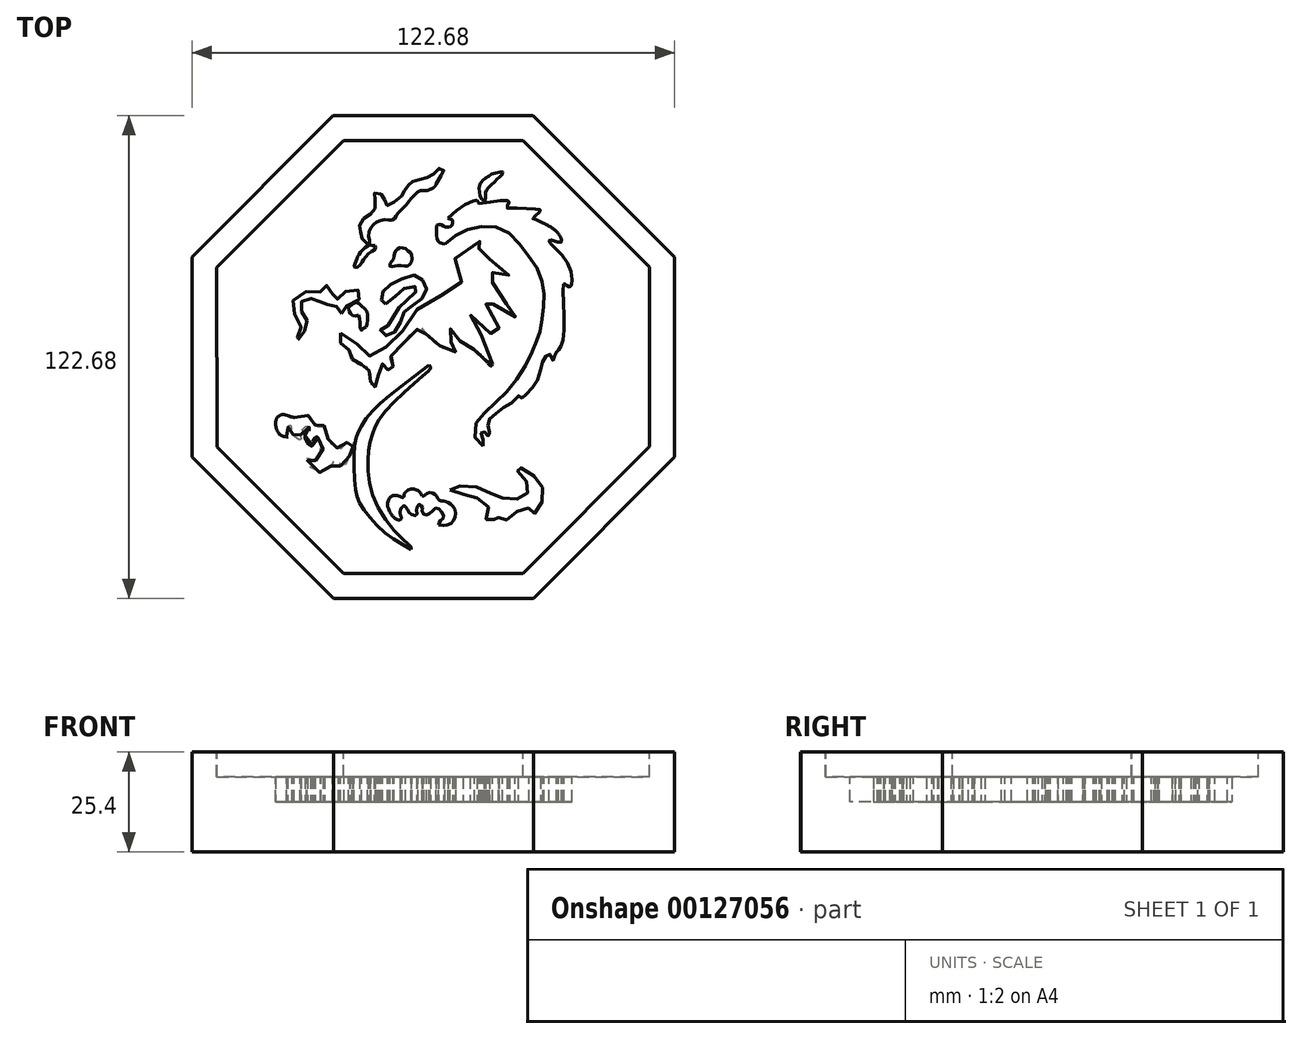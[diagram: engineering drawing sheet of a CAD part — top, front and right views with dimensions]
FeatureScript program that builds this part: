
annotation { "Feature Type Name" : "Feature", "Feature Type Description" : "" }
export const myFeature = defineFeature(function(context is Context, id is Id, definition is map)
    precondition{}
    {
        {
            var Q0;
            Q0=qCreatedBy(makeId("Top.planeOp"),FACE);
            var sketch = newSketch(context, id + "F0", { "sketchPlane" : qUnion([Q0])});
            skCircle(sketch, "E0.cCircle", {"center": v(0, 0) * mm, "radius": 61.32 * mm, "construction": true});
            skLineSegment(sketch, "E0.0", {"start": v(-61.3, -25.44) * mm, "end": v(-61.34, 25.36) * mm});
            skLineSegment(sketch, "E0.1", {"start": v(-61.34, 25.36) * mm, "end": v(-25.44, 61.3) * mm});
            skLineSegment(sketch, "E0.2", {"start": v(-25.44, 61.3) * mm, "end": v(25.36, 61.34) * mm});
            skLineSegment(sketch, "E0.3", {"start": v(25.36, 61.34) * mm, "end": v(61.3, 25.44) * mm});
            skLineSegment(sketch, "E0.4", {"start": v(61.3, 25.44) * mm, "end": v(61.34, -25.36) * mm});
            skLineSegment(sketch, "E0.5", {"start": v(61.34, -25.36) * mm, "end": v(25.44, -61.3) * mm});
            skLineSegment(sketch, "E0.6", {"start": v(25.44, -61.3) * mm, "end": v(-25.36, -61.34) * mm});
            skLineSegment(sketch, "E0.7", {"start": v(-25.36, -61.34) * mm, "end": v(-61.3, -25.44) * mm});
            skPoint(sketch, "E0.0.midPoint", {"position": v(-61.32, -0.04) * mm});
            skSolve(sketch);
        }
        {
            var Q0;
            Q0=qSketchRegion(id+"F0",true);
            extrude(context, id + "F1", {"entities" : qUnion([Q0]), "depth" : 25.4 * mm});
        }
        {
            var Q0;
            Q0=makeQuery(id+"F1.opExtrude","CAP_FACE",FACE,{"disambiguationData":[OSD([sQuery(id+"F0.wireOp",EDGE,"E0.0"),sQuery(id+"F0.wireOp",EDGE,"E0.1"),sQuery(id+"F0.wireOp",EDGE,"E0.2"),sQuery(id+"F0.wireOp",EDGE,"E0.3"),sQuery(id+"F0.wireOp",EDGE,"E0.4"),sQuery(id+"F0.wireOp",EDGE,"E0.5"),sQuery(id+"F0.wireOp",EDGE,"E0.6"),sQuery(id+"F0.wireOp",EDGE,"E0.7")])],"isStart":false});
            var sketch = newSketch(context, id + "F2", { "sketchPlane" : qUnion([Q0])});
            skLineSegment(sketch, "E1.0", {"start": v(-54.96, -22.8) * mm, "end": v(-54.99, 22.73) * mm});
            skLineSegment(sketch, "E1.1", {"start": v(-22.73, -54.99) * mm, "end": v(-54.96, -22.8) * mm});
            skLineSegment(sketch, "E1.2", {"start": v(-54.99, 22.73) * mm, "end": v(-22.8, 54.96) * mm});
            skLineSegment(sketch, "E1.3", {"start": v(22.8, -54.96) * mm, "end": v(-22.73, -54.99) * mm});
            skLineSegment(sketch, "E1.4", {"start": v(-22.8, 54.96) * mm, "end": v(22.73, 54.99) * mm});
            skLineSegment(sketch, "E1.5", {"start": v(22.73, 54.99) * mm, "end": v(54.96, 22.8) * mm});
            skLineSegment(sketch, "E1.6", {"start": v(54.96, 22.8) * mm, "end": v(54.99, -22.73) * mm});
            skLineSegment(sketch, "E1.7", {"start": v(54.99, -22.73) * mm, "end": v(22.8, -54.96) * mm});
            skSolve(sketch);
        }
        {
            var Q0;
            Q0=qSketchRegion(id+"F2",true);
            extrude(context, id + "F3", {"entities" : qUnion([Q0]), "operationType" : NewBodyOperationType.REMOVE, "oppositeDirection" : true, "depth" : 6.35 * mm});
        }
        {
            var Q0;
            Q0=makeQuery(id+"F3.boolean.opBoolean","COPY",FACE,{"derivedFrom":makeQuery(id+"F3.opExtrude","CAP_FACE",FACE,{"disambiguationData":[OSD([sQuery(id+"F2.wireOp",EDGE,"E1.0"),sQuery(id+"F2.wireOp",EDGE,"E1.1"),sQuery(id+"F2.wireOp",EDGE,"E1.2"),sQuery(id+"F2.wireOp",EDGE,"E1.3"),sQuery(id+"F2.wireOp",EDGE,"E1.4"),sQuery(id+"F2.wireOp",EDGE,"E1.5"),sQuery(id+"F2.wireOp",EDGE,"E1.6"),sQuery(id+"F2.wireOp",EDGE,"E1.7")])],"isStart":false})});
            var sketch = newSketch(context, id + "F4", { "sketchPlane" : qUnion([Q0])});
            skFitSpline(sketch, "E2", {"points": [v(-1.1, -2.1) * mm, v(-15.28, -13.56) * mm, v(-18.94, -18.81) * mm, v(-20.03, -22.74) * mm, v(-19.8, -33.28) * mm, v(-18.48, -37.41) * mm, v(-13.16, -43.92) * mm, v(-5.64, -48.87) * mm], "startDerivative": vector(-92.7, -70.76) * mm, "endDerivative": vector(49.7, -26.65) * mm});
            skFitSpline(sketch, "E3", {"points": [v(-1.1, -2.1) * mm, v(-0.63, -2.66) * mm, v(-2.57, -4.73) * mm, v(-12.47, -14.06) * mm, v(-15.53, -19.76) * mm, v(-16.6, -26.27) * mm, v(-13.9, -38.48) * mm, v(-6.27, -47.68) * mm, v(-5.64, -48.3) * mm, v(-5.64, -48.87) * mm], "startDerivative": vector(15.8, -12.08) * mm, "endDerivative": vector(-1.9, -16.76) * mm});
            skFitSpline(sketch, "E4", {"points": [v(-23.56, 6.14) * mm, v(-22.79, 5.01) * mm, v(-21, 4.18) * mm, v(-19.5, 3.43) * mm, v(-18.43, 1.99) * mm, v(-17.94, 0.65) * mm, v(-17.3, 0) * mm, v(-14.98, 0.65) * mm, v(-14.07, 0.65) * mm, v(-12.95, 1.64) * mm, v(-11.75, 2.76) * mm, v(-10.14, 4.24) * mm, v(-9.01, 5.22) * mm, v(-7.25, 7.4) * mm, v(-5.78, 10.07) * mm, v(-4.65, 11.62) * mm, v(-2.2, 13.44) * mm, v(0, 14.85) * mm, v(3.36, 15.97) * mm, v(4.98, 16.19) * mm, v(7.08, 18.79) * mm, v(7.36, 22.72) * mm, v(6.33, 24.4) * mm, v(5.33, 25.33) * mm, v(9.1, 28.92) * mm, v(12.6, 29.34) * mm, v(14.27, 29.34) * mm, v(12.35, 28.27) * mm, v(11.37, 27.15) * mm, v(11.16, 25.95) * mm, v(12.64, 25.18) * mm, v(14.32, 24.83) * mm, v(17.2, 23.5) * mm, v(18.54, 21.95) * mm, v(19.31, 20.26) * mm, v(18.6, 20.4) * mm, v(17, 20.96) * mm, v(14.81, 21.46) * mm, v(13.48, 20.75) * mm, v(13.34, 20.05) * mm, v(13.69, 19.63) * mm, v(15.66, 18.5) * mm, v(17.27, 16.4) * mm, v(18.33, 14) * mm, v(20.09, 12.04) * mm, v(21.5, 10.84) * mm, v(21.5, 10.28) * mm, v(20.37, 10.28) * mm, v(18.05, 11.05) * mm, v(15.52, 13.1) * mm, v(14.46, 14.36) * mm, v(13.48, 15.06) * mm, v(12.99, 14.92) * mm, v(13.34, 13.51) * mm, v(14.6, 11.2) * mm, v(16.43, 9.02) * mm, v(16.64, 4.59) * mm, v(16.71, 3.96) * mm, v(15.52, 5.01) * mm, v(12.28, 8.17) * mm, v(10.25, 10.42) * mm, v(9.47, 10.63) * mm, v(9.61, 9.23) * mm, v(10.74, 7.61) * mm, v(12.28, 5.43) * mm, v(13.55, 3.75) * mm, v(15.1, -1.8) * mm], "startDerivative": vector(44.12, -97.76) * mm, "endDerivative": vector(53.66, -252.27) * mm});
            skFitSpline(sketch, "E5", {"points": [v(-23.56, 6.14) * mm, v(-23.97, 5.3) * mm, v(-24, 4.48) * mm, v(-23.56, 3.64) * mm, v(-22.79, 2.98) * mm, v(-22.5, 2.67) * mm, v(-21.65, 1.95) * mm, v(-20.68, 1.41) * mm, v(-20.65, 0.63) * mm, v(-20.62, -0.28) * mm, v(-20.21, -1.4) * mm, v(-19, -1.8) * mm, v(-18.27, -1.84) * mm, v(-17.37, -2.22) * mm, v(-16.77, -2.6) * mm, v(-16.43, -3.22) * mm, v(-16.18, -3.78) * mm, v(-15.86, -4.75) * mm, v(-15.99, -6.04) * mm, v(-15.83, -7.38) * mm, v(-15.83, -7.7) * mm, v(-15.42, -7.73) * mm, v(-14.64, -7.44) * mm, v(-14.08, -5.91) * mm, v(-14.08, -4.9) * mm, v(-13.55, -3.69) * mm, v(-13.67, -2.56) * mm, v(-12.95, -1.78) * mm, v(-12.51, -1.75) * mm, v(-12.14, -2.25) * mm, v(-11.82, -2.62) * mm, v(-11.42, -3.4) * mm, v(-11.23, -3.72) * mm, v(-10.32, -3.4) * mm, v(-10.2, -2.72) * mm, v(-10.45, -1.68) * mm, v(-10.98, -0.59) * mm, v(-10.89, 0) * mm, v(-10.42, 0.76) * mm, v(-8.32, 2.6) * mm, v(-6.16, 5.36) * mm, v(-4.15, 7.02) * mm, v(-3.3, 7.55) * mm, v(-2.18, 6.58) * mm, v(-1.3, 5.01) * mm, v(0.82, 3.58) * mm, v(3.2, 1.92) * mm, v(5.49, 1.32) * mm, v(5.74, 1.38) * mm, v(5.43, 1.92) * mm, v(4.92, 2.92) * mm, v(4.33, 4.36) * mm, v(4.14, 6.42) * mm, v(4.33, 7.14) * mm, v(4.58, 6.92) * mm, v(5.7, 5.45) * mm, v(7.59, 3.42) * mm, v(9.5, 2.57) * mm, v(10.68, 1.6) * mm, v(12.22, 0.26) * mm, v(13.66, -1.28) * mm, v(14.28, -2.03) * mm, v(14.66, -2.31) * mm, v(15.1, -1.8) * mm], "startDerivative": vector(-33.8, -56.96) * mm, "endDerivative": vector(35.19, 59.41) * mm});
            skFitSpline(sketch, "E6", {"points": [v(3.02, 28.65) * mm, v(5.32, 30.69) * mm, v(7.88, 32.02) * mm, v(10.9, 32.95) * mm, v(14.44, 33.25) * mm, v(17.73, 32.4) * mm, v(20.66, 30.25) * mm, v(22.82, 27.45) * mm, v(25.17, 24.43) * mm, v(26.96, 21.56) * mm, v(27.82, 18.27) * mm, v(28.13, 15.75) * mm, v(27.98, 13.3) * mm, v(27.83, 10.88) * mm, v(27.4, 8.1) * mm, v(26.94, 5.85) * mm, v(26.35, 4.26) * mm, v(25.69, 2.62) * mm, v(24.16, -0.73) * mm, v(22.41, -3.85) * mm, v(19.64, -7.82) * mm, v(17.33, -10.23) * mm, v(14.4, -12.82) * mm, v(11.7, -15.6) * mm, v(10.6, -17.65) * mm, v(10.86, -21.09) * mm, v(12.7, -22.63) * mm], "startDerivative": vector(58.67, 60.1) * mm, "endDerivative": vector(54.1, -50.25) * mm});
            skFitSpline(sketch, "E7", {"points": [v(3.02, 28.65) * mm, v(1.21, 29.42) * mm, v(0.86, 31.3) * mm, v(0.86, 33.34) * mm, v(1.65, 33.7) * mm, v(3.02, 33.08) * mm, v(3.77, 33.02) * mm, v(4.67, 33.34) * mm, v(4.84, 34.4) * mm, v(4.58, 35.03) * mm, v(3.77, 35.11) * mm, v(3.77, 35.26) * mm], "startDerivative": vector(-14.7, 5.6) * mm, "endDerivative": vector(3.92, 12.76) * mm});
            skFitSpline(sketch, "E8", {"points": [v(12.7, -22.63) * mm, v(12.7, -21.63) * mm, v(12.7, -20.6) * mm, v(12.09, -19.6) * mm, v(12.7, -18.76) * mm, v(12.88, -18.81) * mm, v(13.13, -19.2) * mm, v(13.64, -19.76) * mm, v(13.97, -20.1) * mm, v(14.17, -20.15) * mm, v(14.33, -19.37) * mm, v(14.1, -18.73) * mm, v(13.89, -17.28) * mm, v(14.14, -16.25) * mm, v(14.44, -15.44) * mm, v(16.26, -14.21) * mm, v(17.7, -12.93) * mm, v(19.46, -11.92) * mm, v(21.25, -10.53) * mm, v(21.97, -9.47) * mm, v(22.48, -10.33) * mm, v(22.92, -10.22) * mm, v(23.45, -9.6) * mm, v(24.71, -8.3) * mm, v(26.14, -6.56) * mm, v(26.77, -5.21) * mm, v(27.5, -2.3) * mm, v(27.8, -1.3) * mm, v(28.3, -0.29) * mm, v(28.95, 0.66) * mm, v(29.48, 0.97) * mm, v(29.93, 0) * mm, v(30.32, -0.9) * mm, v(30.5, -0.74) * mm, v(30.64, -0.37) * mm, v(30.85, 0.34) * mm, v(31.3, 0.76) * mm, v(31.3, 1.37) * mm, v(31.4, 2.13) * mm, v(31.82, 1.82) * mm], "startDerivative": vector(114.89, 72.43) * mm, "endDerivative": vector(25.79, -28.95) * mm});
            skFitSpline(sketch, "E9", {"points": [v(4.22, -33.74) * mm, v(5.24, -33) * mm, v(6.7, -32.76) * mm, v(9.3, -32.8) * mm, v(12.64, -33.55) * mm, v(14.72, -34.69) * mm, v(16.3, -35.4) * mm, v(17.95, -35.9) * mm, v(20.3, -35.9) * mm, v(22.31, -36.1) * mm, v(23.61, -34.96) * mm, v(24.36, -33.47) * mm, v(23.73, -31.7) * mm, v(22.63, -30.48) * mm, v(21.17, -28.7) * mm, v(20.74, -28.2) * mm, v(21.69, -28.08) * mm, v(24.12, -28.98) * mm, v(25.97, -30.64) * mm, v(27.47, -32.56) * mm, v(27.94, -34.33) * mm, v(27.59, -36.93) * mm, v(26.88, -38.98) * mm, v(25.46, -39.76) * mm, v(25.27, -39.17) * mm, v(24.44, -38.47) * mm, v(23.26, -38.5) * mm, v(21.57, -39.01) * mm, v(19.84, -40.47) * mm, v(18.34, -41.57) * mm, v(17.16, -41.8) * mm, v(16.57, -40.94) * mm, v(16.77, -40.2) * mm, v(16.14, -40.83) * mm, v(14.96, -41.45) * mm, v(13.93, -41.7) * mm, v(13.42, -41.45) * mm, v(14.01, -40.08) * mm, v(14.05, -38.3) * mm, v(12.64, -36.62) * mm, v(10.43, -35.55) * mm, v(8.7, -35.16) * mm, v(5.71, -34.25) * mm, v(4.22, -33.74) * mm]});
            skFitSpline(sketch, "E10", {"points": [v(-16.67, 28.7) * mm, v(-18, 29.86) * mm, v(-18.45, 31.27) * mm, v(-18.63, 32.43) * mm, v(-18.66, 33.6) * mm, v(-17.71, 35.17) * mm, v(-16.1, 36.3) * mm, v(-14.92, 37.3) * mm, v(-14.86, 39.03) * mm, v(-14.86, 40.76) * mm, v(-14.9, 41.74) * mm, v(-13.33, 41.43) * mm, v(-12.62, 40.38) * mm, v(-12.24, 39.5) * mm, v(-11.66, 38.45) * mm, v(-10.2, 39.25) * mm, v(-8.16, 40.86) * mm, v(-7.43, 41.96) * mm, v(-6.98, 42.66) * mm, v(-6.14, 43.86) * mm, v(-5.7, 44.4) * mm, v(-4.58, 44.7) * mm, v(-3.1, 45.2) * mm, v(-1.5, 45.65) * mm, v(0, 46.43) * mm, v(1.04, 47.5) * mm, v(2.13, 48.13) * mm, v(2.67, 47.16) * mm, v(2.22, 46.36) * mm, v(1.24, 44.58) * mm, v(-2.4, 42.29) * mm], "startDerivative": vector(-45.56, 30.18) * mm, "endDerivative": vector(-81.9, 12.02) * mm});
            skFitSpline(sketch, "E11", {"points": [v(0.71, 43.88) * mm, v(0.34, 43.3) * mm, v(-0.41, 42.74) * mm, v(-1.53, 42.46) * mm, v(-2.4, 42.29) * mm, v(-3.32, 42.29) * mm, v(-4.04, 41.81) * mm, v(-5.02, 40.84) * mm, v(-5.86, 39.97) * mm, v(-6.67, 38.85) * mm, v(-7.73, 37.8) * mm, v(-8.68, 36.78) * mm, v(-9.24, 36.28) * mm, v(-9.66, 35.22) * mm, v(-9.97, 35.2) * mm, v(-10.61, 34.74) * mm, v(-11.9, 34.91) * mm, v(-13.27, 34.69) * mm, v(-14.36, 34.3) * mm, v(-15.3, 33.4) * mm, v(-16.12, 32.37) * mm, v(-16.5, 30.64) * mm, v(-16.15, 29.52) * mm, v(-16.2, 28.62) * mm, v(-16.67, 28.7) * mm], "startDerivative": vector(-10.07, -14.43) * mm, "endDerivative": vector(-22.91, 7.23) * mm});
            skFitSpline(sketch, "E12", {"points": [v(-14.81, 28.31) * mm, v(-15.35, 28.37) * mm, v(-16.1, 28.42) * mm, v(-16.69, 28.2) * mm, v(-17.58, 27.56) * mm, v(-18.34, 26.75) * mm, v(-18.78, 26.05) * mm, v(-19.23, 25.46) * mm, v(-19.31, 24.99) * mm, v(-19.6, 24.29) * mm, v(-19.96, 23.62) * mm, v(-20.07, 22.83) * mm, v(-19.96, 22.78) * mm, v(-19.34, 22.78) * mm, v(-18.56, 23.45) * mm, v(-17.92, 24.48) * mm, v(-17.39, 25.18) * mm, v(-16.02, 26.6) * mm, v(-15.1, 27.05) * mm, v(-14.65, 27.84) * mm, v(-14.81, 28.31) * mm]});
            skFitSpline(sketch, "E13", {"points": [v(-8.41, 27.75) * mm, v(-9.11, 27.47) * mm, v(-9.64, 26.89) * mm, v(-9.9, 26.33) * mm, v(-9.92, 25.77) * mm, v(-10.04, 25.01) * mm, v(-10.34, 24.57) * mm, v(-10.85, 23.87) * mm, v(-11.07, 23.14) * mm, v(-10.76, 23) * mm, v(-10.18, 22.97) * mm, v(-9.4, 23.23) * mm, v(-8.61, 23.25) * mm, v(-7.66, 23.14) * mm, v(-6.68, 23.11) * mm, v(-6.2, 23.37) * mm, v(-5.65, 23.9) * mm, v(-5.37, 24.8) * mm, v(-5.45, 25.85) * mm, v(-5.7, 26.47) * mm, v(-6.35, 26.92) * mm, v(-7.13, 27.56) * mm, v(-7.74, 27.73) * mm, v(-8.41, 27.75) * mm]});
            skFitSpline(sketch, "E14", {"points": [v(-12.08, 13.51) * mm, v(-12.69, 13.42) * mm, v(-12.92, 13.6) * mm, v(-13.25, 14.26) * mm, v(-12.97, 14.78) * mm, v(-13.02, 15.72) * mm, v(-12.78, 16.61) * mm, v(-11.75, 17.88) * mm, v(-11.23, 18.16) * mm, v(-10.1, 18.77) * mm, v(-8.61, 19.57) * mm, v(-7.05, 20.14) * mm, v(-5.17, 20.7) * mm, v(-4.32, 20.84) * mm, v(-3.15, 20.14) * mm, v(-2.54, 19.24) * mm, v(-2.2, 18.5) * mm, v(-1.69, 17.13) * mm, v(-1.88, 16) * mm, v(-2.68, 14.97) * mm, v(-3.95, 13.93) * mm, v(-5.21, 13.13) * mm, v(-6.1, 12.52) * mm, v(-7.19, 11.68) * mm, v(-7.56, 10.74) * mm, v(-7.85, 9.42) * mm, v(-8.61, 8.53) * mm, v(-9.26, 6.93) * mm, v(-10.2, 6.04) * mm, v(-11.14, 5.47) * mm, v(-11.94, 5.43) * mm, v(-13.06, 5.61) * mm, v(-13.35, 6.23) * mm, v(-13.44, 6.98) * mm, v(-12.97, 7.5) * mm, v(-11.84, 7.87) * mm, v(-10.76, 8.58) * mm, v(-10.48, 9.19) * mm, v(-9.82, 10.93) * mm, v(-9.44, 11.72) * mm, v(-8.61, 12.71) * mm, v(-7.9, 13.46) * mm, v(-7.05, 14.12) * mm, v(-5.83, 15.25) * mm, v(-4.65, 16.33) * mm, v(-3.9, 17.27) * mm, v(-3.95, 17.79) * mm, v(-4.74, 17.93) * mm, v(-6.58, 17.98) * mm, v(-7.52, 17.32) * mm, v(-8.61, 16.57) * mm, v(-9.82, 15.3) * mm, v(-11, 14.45) * mm, v(-12.08, 13.51) * mm]});
            skFitSpline(sketch, "E15", {"points": [v(-23.31, 11.08) * mm, v(-22.75, 11.21) * mm, v(-22.61, 11.88) * mm, v(-22.55, 12.5) * mm, v(-22.08, 12.9) * mm, v(-20.82, 13.57) * mm, v(-20.09, 14.07) * mm, v(-19, 14.57) * mm, v(-18.3, 15.2) * mm, v(-18.36, 16.06) * mm, v(-18.63, 16.53) * mm, v(-19.2, 17.03) * mm, v(-20.39, 17.1) * mm, v(-21.22, 16.83) * mm, v(-22.18, 16.73) * mm, v(-22.68, 16.46) * mm, v(-23.15, 16.06) * mm, v(-23.98, 15.27) * mm, v(-24.4, 14.67) * mm, v(-24.77, 14.5) * mm, v(-25.44, 14.9) * mm, v(-25.57, 15.27) * mm, v(-25.54, 15.73) * mm, v(-25.7, 16.4) * mm, v(-25.77, 17.23) * mm, v(-26.27, 17.93) * mm, v(-26.97, 18.16) * mm, v(-27.8, 18.03) * mm, v(-28.56, 17.53) * mm, v(-28.56, 16.96) * mm, v(-28.66, 16.6) * mm, v(-29.03, 16.6) * mm, v(-30.92, 16.63) * mm, v(-31.69, 16.7) * mm, v(-33.28, 16.46) * mm, v(-34.88, 15.3) * mm, v(-35.58, 14.37) * mm, v(-35.9, 13.07) * mm, v(-35.54, 11.55) * mm, v(-35.24, 10.91) * mm, v(-34.51, 9.58) * mm, v(-33.95, 8.82) * mm, v(-33.61, 7.62) * mm, v(-33.75, 6.96) * mm, v(-33.95, 6.23) * mm, v(-34.25, 5.66) * mm, v(-34.51, 5.03) * mm, v(-34.91, 4.6) * mm, v(-35.34, 4) * mm, v(-34.91, 4.2) * mm, v(-34.21, 4.53) * mm, v(-33.68, 5) * mm, v(-33.38, 5.5) * mm, v(-33.12, 5.86) * mm, v(-32.72, 6.56) * mm, v(-32.32, 7.3) * mm, v(-32.19, 7.82) * mm, v(-32.19, 8.49) * mm, v(-32.12, 9.32) * mm, v(-32.22, 10.08) * mm, v(-32.58, 10.71) * mm, v(-33.05, 11.05) * mm, v(-33.55, 11.78) * mm, v(-33.78, 12.4) * mm, v(-33.85, 12.94) * mm, v(-33.78, 13.64) * mm, v(-33.45, 14.07) * mm, v(-32.95, 14.44) * mm, v(-32.62, 14.54) * mm, v(-31.82, 14.74) * mm, v(-31.12, 14.9) * mm, v(-30.56, 14.8) * mm, v(-30.52, 14.77) * mm, v(-29.86, 14.6) * mm, v(-29.7, 14.57) * mm, v(-29.3, 14.34) * mm, v(-28.63, 14.04) * mm, v(-28.6, 14) * mm, v(-28, 13.77) * mm, v(-27.87, 13.7) * mm, v(-27.1, 13.4) * mm, v(-26.83, 13.34) * mm, v(-26.27, 13.2) * mm, v(-26.1, 13.14) * mm, v(-25.3, 13) * mm, v(-25.1, 13) * mm, v(-24.5, 12.74) * mm, v(-24.08, 12.44) * mm, v(-23.84, 12.08) * mm, v(-23.58, 11.68) * mm, v(-23.44, 11.51) * mm, v(-23.31, 11.08) * mm]});
            skFitSpline(sketch, "E16", {"points": [v(-18.97, 10.68) * mm, v(-19.53, 10.46) * mm, v(-20.05, 10.5) * mm, v(-20.64, 10.64) * mm, v(-21.04, 11) * mm, v(-21.31, 11.5) * mm, v(-21.44, 12.02) * mm, v(-21.55, 12.55) * mm, v(-21.34, 12.9) * mm, v(-21.15, 13.04) * mm, v(-20.9, 13.08) * mm, v(-20.48, 13.51) * mm, v(-20.16, 13.66) * mm, v(-19.77, 13.8) * mm, v(-19.22, 13.7) * mm, v(-18.68, 13.47) * mm, v(-18, 12.79) * mm, v(-17.39, 12.28) * mm, v(-16.84, 11.5) * mm, v(-16.72, 10.9) * mm, v(-16.74, 9.32) * mm, v(-16.8, 8.27) * mm, v(-17.08, 7.66) * mm, v(-17.5, 7.31) * mm, v(-18.05, 7.18) * mm, v(-18.31, 6.73) * mm, v(-18.55, 7.39) * mm, v(-18.64, 8.8) * mm, v(-18.8, 9.95) * mm, v(-18.97, 10.68) * mm]});
            skFitSpline(sketch, "E17", {"points": [v(3.77, 35.26) * mm, v(11.08, 39.86) * mm, v(11.32, 39.5) * mm, v(11.56, 39.07) * mm, v(12.2, 39.02) * mm, v(19.13, 39.71) * mm, v(19.1, 39.03) * mm, v(18.8, 37.84) * mm, v(19.33, 37.81) * mm, v(26.7, 37.5) * mm, v(27.2, 37.17) * mm, v(25.34, 35.26) * mm, v(27.17, 34.5) * mm, v(31.86, 30.1) * mm], "startDerivative": vector(48.47, 53.5) * mm, "endDerivative": vector(-17.45, 9.61) * mm});
            skFitSpline(sketch, "E18", {"points": [v(31.82, 1.82) * mm, v(33.14, 5.57) * mm, v(33.14, 18.6) * mm, v(33.4, 18.6) * mm, v(33.83, 18.29) * mm, v(34.62, 17.81) * mm, v(35.04, 18.13) * mm, v(34.3, 23.61) * mm, v(29.6, 29.1) * mm, v(29.5, 29.63) * mm, v(30.3, 29.68) * mm, v(31.3, 29.26) * mm, v(32.51, 29.2) * mm, v(32.62, 29.7) * mm], "startDerivative": vector(15.65, 22.15) * mm, "endDerivative": vector(4.85, 24.2) * mm});
            skFitSpline(sketch, "E19", {"points": [v(32.62, 29.7) * mm, v(27.92, 34.03) * mm], "startDerivative": vector(-1.32, 4.65) * mm, "endDerivative": vector(-8.93, 3.87) * mm});
            skFitSpline(sketch, "E20", {"points": [v(13.13, 39.65) * mm, v(13.2, 40.3) * mm, v(13.28, 41.09) * mm, v(13.33, 41.84) * mm, v(13.5, 42.4) * mm, v(14.1, 43.18) * mm, v(15.27, 44.18) * mm, v(16.15, 45.15) * mm, v(16.92, 45.8) * mm, v(17.59, 46.62) * mm, v(17.59, 47.06) * mm, v(17.07, 46.94) * mm, v(15.12, 46.67) * mm, v(14.3, 46.14) * mm, v(13.16, 45.37) * mm, v(12.09, 44.35) * mm, v(11.66, 42.9) * mm, v(11.79, 41.56) * mm, v(12.31, 40.12) * mm, v(13.13, 39.65) * mm]});
            skFitSpline(sketch, "E21", {"points": [v(-8, -35.63) * mm, v(-11.58, -38) * mm], "startDerivative": vector(-2.13, 1.07) * mm, "endDerivative": vector(0.53, -11.81) * mm});
            skFitSpline(sketch, "E22", {"points": [v(-8, -35.63) * mm, v(-7.55, -35.63) * mm, v(-7.43, -34.94) * mm, v(-6.4, -33.81) * mm, v(-4.65, -33.6) * mm, v(-3.37, -34.4) * mm, v(-2.84, -35.27) * mm], "startDerivative": vector(4.97, -1.27) * mm, "endDerivative": vector(4.53, -4.84) * mm});
            skFitSpline(sketch, "E23", {"points": [v(-2.75, -35.27) * mm, v(-2.33, -35.27) * mm, v(-2.04, -34.9) * mm, v(-0.8, -34.43) * mm, v(0.5, -35) * mm, v(0.98, -35.68) * mm, v(1.6, -36.48) * mm, v(2.55, -36.6) * mm, v(3.5, -36.86) * mm, v(5, -37.93) * mm, v(5.63, -40.1) * mm, v(4.4, -42.32) * mm, v(1.37, -42.74) * mm], "startDerivative": vector(9.14, -1.93) * mm, "endDerivative": vector(-25.98, 3.75) * mm});
            skFitSpline(sketch, "E24", {"points": [v(1.37, -42.74) * mm, v(1.37, -42.34) * mm, v(1.8, -41.63) * mm, v(2.37, -41.13) * mm, v(2.6, -40.18) * mm, v(1.84, -39.02) * mm, v(0.83, -38.34) * mm, v(-0.41, -39.26) * mm, v(-1.27, -40) * mm, v(-2.3, -40.03) * mm, v(-2.78, -39.3) * mm, v(-2.78, -38.52) * mm, v(-2.99, -37.81) * mm, v(-3.5, -37.43) * mm, v(-4.03, -37.96) * mm, v(-4.3, -39.02) * mm, v(-4.23, -40.15) * mm, v(-4.91, -40.24) * mm, v(-6.04, -39.73) * mm, v(-6.54, -38.76) * mm, v(-7.05, -38.08) * mm], "startDerivative": vector(-1.83, 11.28) * mm, "endDerivative": vector(-11.47, 13.55) * mm});
            skFitSpline(sketch, "E25", {"points": [v(-7.05, -38.08) * mm, v(-8.32, -38.67) * mm], "startDerivative": vector(-0.53, 1.07) * mm, "endDerivative": vector(-2.13, -3.2) * mm});
            skFitSpline(sketch, "E26", {"points": [v(-8.32, -38.67) * mm, v(-8.08, -40.95) * mm], "startDerivative": vector(-0.8, -4.35) * mm, "endDerivative": vector(0.47, -2.37) * mm});
            skFitSpline(sketch, "E27", {"points": [v(-11.58, -38) * mm, v(-8.56, -41.4) * mm, v(-8.08, -40.95) * mm], "startDerivative": vector(3.55, -11) * mm, "endDerivative": vector(1.4, 2.48) * mm});
            skFitSpline(sketch, "E28", {"points": [v(-37.32, -20.2) * mm, v(-40.05, -17.12) * mm], "startDerivative": vector(-3.29, -0.44) * mm, "endDerivative": vector(-0.44, 7.28) * mm});
            skFitSpline(sketch, "E29", {"points": [v(-40.05, -17.12) * mm, v(-37.95, -14.58) * mm], "startDerivative": vector(-0.53, 6.66) * mm, "endDerivative": vector(1.42, -0.09) * mm});
            skFitSpline(sketch, "E30", {"points": [v(-37.95, -14.58) * mm, v(-36.82, -14.81) * mm, v(-36.32, -15.4) * mm, v(-35.7, -15.5) * mm, v(-35.1, -15.28) * mm, v(-34.4, -14.78) * mm, v(-32.91, -14.58) * mm, v(-31.26, -15.17) * mm, v(-30.6, -15.9) * mm, v(-30.07, -16.8) * mm, v(-30.01, -17.3) * mm, v(-29.92, -17.89) * mm, v(-29.39, -17.65) * mm, v(-28.38, -17.42) * mm, v(-27.67, -17.48) * mm, v(-27.76, -18.45) * mm, v(-27.26, -19.78) * mm, v(-26.58, -21.12) * mm, v(-26.07, -21.92) * mm, v(-25.33, -22.86) * mm, v(-24.12, -23.13) * mm, v(-22.85, -23.16) * mm, v(-22.34, -22.69) * mm, v(-21.93, -21.65) * mm, v(-21.3, -21.18) * mm, v(-20.54, -21.47) * mm, v(-20.36, -22.48) * mm, v(-20.5, -23.16) * mm, v(-20.5, -23.81) * mm, v(-21.1, -24.02) * mm, v(-21.3, -24.94) * mm, v(-21.22, -26.33) * mm, v(-22.02, -27.22) * mm, v(-23.97, -27.57) * mm, v(-25.63, -26.6) * mm, v(-25.84, -26.6) * mm, v(-25.98, -27.4) * mm, v(-26.28, -28.37) * mm, v(-27.29, -29.17) * mm, v(-28.68, -29.35) * mm, v(-30.6, -28.49) * mm, v(-31.9, -26.83) * mm, v(-31.94, -25.82) * mm, v(-31.73, -25.38) * mm, v(-31.5, -25.65) * mm, v(-30.16, -26.27) * mm, v(-29.18, -26) * mm, v(-28.89, -24.82) * mm, v(-28.06, -23.52) * mm, v(-28.24, -22.86) * mm, v(-28.86, -22.36) * mm, v(-29.03, -21.44) * mm, v(-29.5, -20.29) * mm, v(-30.4, -20.9) * mm, v(-30.6, -21.5) * mm, v(-30.72, -22.54) * mm, v(-31.5, -22.33) * mm, v(-32.3, -21.3) * mm, v(-32.56, -19.9) * mm, v(-31.94, -18.66) * mm, v(-31.14, -18.36) * mm, v(-31.31, -18.16) * mm, v(-31.64, -17.74) * mm, v(-32.38, -17.68) * mm, v(-33.42, -18.63) * mm, v(-33.71, -19.87) * mm, v(-33.65, -21) * mm, v(-34.9, -20.52) * mm, v(-35.81, -19.34) * mm, v(-35.96, -17.98) * mm, v(-36.2, -17.39) * mm, v(-36.85, -17.68) * mm, v(-37.2, -18.9) * mm, v(-37.09, -20.02) * mm, v(-37, -20.35) * mm, v(-37.32, -20.2) * mm], "startDerivative": vector(98.05, -6.6) * mm, "endDerivative": vector(-54.45, 32.82) * mm});
            skFitSpline(sketch, "E31", {"points": [v(-2.84, -35.27) * mm, v(-2.75, -35.27) * mm], "startDerivative": vector(0.1, 0) * mm, "endDerivative": vector(0.1, 0) * mm});
            skSolve(sketch);
        }
        {
            var Q0;
            Q0 = qSketchRegion(id + "F4", true);
            extrude(context, id + "F5", {"entities" : qUnion([Q0]), "operationType" : NewBodyOperationType.REMOVE, "oppositeDirection" : true, "depth" : 6.35 * mm});
        }
        {
            var Q0;
            Q0 = qSketchRegion(id + "F4", true);
            extrude(context, id + "F6", {"entities" : qUnion([Q0]), "operationType" : NewBodyOperationType.REMOVE, "oppositeDirection" : true, "depth" : 6.35 * mm});
        }
    });
